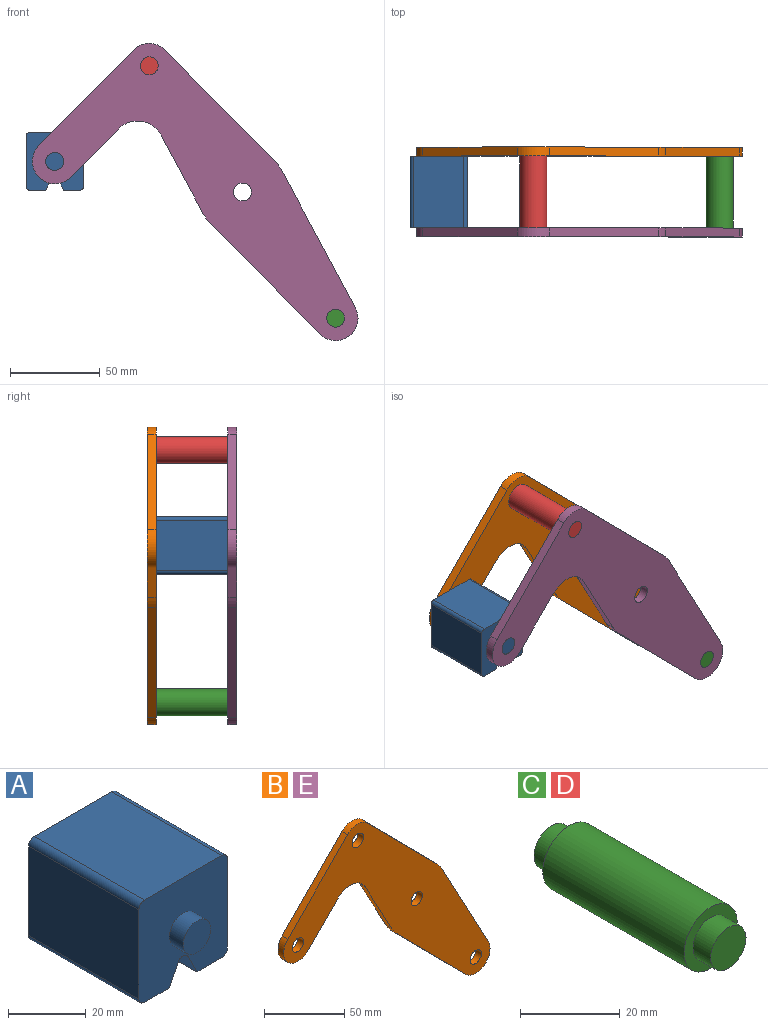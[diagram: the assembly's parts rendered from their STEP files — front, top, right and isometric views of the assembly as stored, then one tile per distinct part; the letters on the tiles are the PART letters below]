
ASSEMBLY  parts=5 mates=3
PART A: 18 faces, bbox 32.1x50x32.1 mm
  f0: plane 40x28.08mm, normal (1,0,0), area 1123.1mm2, adj f4,f10,f13,f14
  f1: plane 40x9.04mm, normal (0,0,-1), area 361.6mm2, adj f2,f4,f10,f14
  f2: plane 40x6.42mm, normal (-0.89,0,-0.45), area 287.2mm2, adj f1,f4,f10,f15
  f3: plane 40x6.42mm, normal (0.89,0,-0.45), area 287.2mm2, adj f4,f5,f10,f15
  f4: plane 32.08x32.08mm, normal (0,-1,0), area 900.6mm2, adj f0,f1,f2,f3,f5,f6,f7,f9
  f5: plane 40x9.04mm, normal (0,0,-1), area 361.6mm2, adj f3,f4,f10,f16
  f6: plane 40x28.08mm, normal (0,0,1), area 1123.1mm2, adj f4,f10,f13,f17
  f7: plane 40x28.08mm, normal (-1,0,0), area 1123.1mm2, adj f4,f10,f16,f17
  f8: plane 10x10mm, normal (0,-1,0), area 78.5mm2, adj f9
  f9: cylinder r=5mm len=10mm, axis (0,1,0), area 157.1mm2, adj f4,f8
  f10: plane 32.08x32.08mm, normal (0,1,0), area 900.6mm2, adj f0,f1,f2,f3,f5,f6,f7,f12
  f11: plane 10x10mm, normal (0,1,0), area 78.5mm2, adj f12
  f12: cylinder r=5mm len=10mm, axis (0,-1,0), area 157.1mm2, adj f10,f11
  f13: cylinder r=2mm len=40mm, axis (0,1,0), area 125.7mm2, adj f0,f4,f6,f10
  f14: cylinder r=2mm len=40mm, axis (0,-1,0), area 125.7mm2, adj f0,f1,f4,f10
  f15: cylinder r=2mm len=40mm, axis (0,1,0), area 177.1mm2, adj f2,f3,f4,f10
  f16: cylinder r=2mm len=40mm, axis (0,1,0), area 125.7mm2, adj f4,f5,f7,f10
  f17: cylinder r=2mm len=40mm, axis (0,-1,0), area 125.7mm2, adj f4,f6,f7,f10
PART B: 18 faces, bbox 181.7x5x165.8 mm
  f0: plane 43.49x23.35mm, normal (-0.88,0,-0.47), area 246.8mm2, adj f1,f14,f16,f17
  f1: cylinder r=25mm len=5.75mm, axis (0,1,0), area 35.8mm2, adj f0,f2,f16,f17
  f2: plane 61.6x60.87mm, normal (-0.71,0,-0.7), area 433mm2, adj f1,f3,f16,f17
  f3: cylinder r=12.5mm len=21.39mm, axis (0,1,0), area 178.4mm2, adj f2,f4,f16,f17
  f4: plane 76.3x40.96mm, normal (0.88,0,0.47), area 433mm2, adj f3,f5,f16,f17
  f5: cylinder r=25mm len=5.75mm, axis (0,1,0), area 35.8mm2, adj f4,f6,f16,f17
  f6: plane 61.6x60.87mm, normal (0.71,0,0.7), area 433mm2, adj f5,f7,f16,f17
  f7: cylinder r=12.5mm len=17.78mm, axis (0,1,0), area 98.9mm2, adj f6,f8,f16,f17
  f8: plane 53.35x52.71mm, normal (-0.71,0,0.7), area 375mm2, adj f7,f9,f16,f17
  f9: cylinder r=12.5mm len=21.39mm, axis (0,1,0), area 196.3mm2, adj f8,f10,f16,f17
  f10: plane 26.86x26.54mm, normal (0.71,0,-0.7), area 188.8mm2, adj f9,f14,f16,f17
  f11: cylinder r=5mm len=10mm, axis (0,1,0), area 157.1mm2, adj f16,f17
  f12: cylinder r=5mm len=10mm, axis (0,1,0), area 157.1mm2, adj f16,f17
  f13: cylinder r=5mm len=10mm, axis (0,1,0), area 157.1mm2, adj f16,f17
  f14: cylinder r=15mm len=23.89mm, axis (0,1,0), area 140.2mm2, adj f0,f10,f16,f17
  f15: cylinder r=5mm len=10mm, axis (0,1,0), area 157.1mm2, adj f16,f17
  f16: plane 181.66x165.78mm, normal (0,-1,0), area 8710.1mm2, adj f0,f1,f2,f3,f4,f5,f6,f7
  f17: plane 181.66x165.78mm, normal (0,1,0), area 8710.1mm2, adj f0,f1,f2,f3,f4,f5,f6,f7
PART C: 7 faces, bbox 15x50x15 mm
  f0: cylinder r=7.5mm len=40mm, axis (0,-1,0), area 1885mm2, adj f2,f5
  f1: cylinder r=5mm len=10mm, axis (0,1,0), area 157.1mm2, adj f2,f3
  f2: plane 15x15mm, normal (0,-1,0), area 98.2mm2, adj f0,f1
  f3: plane 10x10mm, normal (0,-1,0), area 78.5mm2, adj f1
  f4: cylinder r=5mm len=10mm, axis (0,-1,0), area 157.1mm2, adj f5,f6
  f5: plane 15x15mm, normal (0,1,0), area 98.2mm2, adj f0,f4
  f6: plane 10x10mm, normal (0,1,0), area 78.5mm2, adj f4
PART D: same geometry as C
PART E: same geometry as B
PLACE A t=(0,-20,0)mm
PLACE B t=(0,25,0)mm
PLACE C t=(103.95,-20,-140.78)mm
PLACE D t=(0,-20,0)mm
PLACE E t=(0,-20,0)mm fixed
MATE revolute E.f9 <-> A.f9  axis (0,1,0) through (-104.69,-20,17.04)mm
MATE fastened C.f0 <-> E.f3  axis (0,-1,0) through (51.98,-20,-70.39)mm
MATE fastened B.f7 <-> D.f0  axis (0,-1,0) through (-51.98,20,70.39)mm
